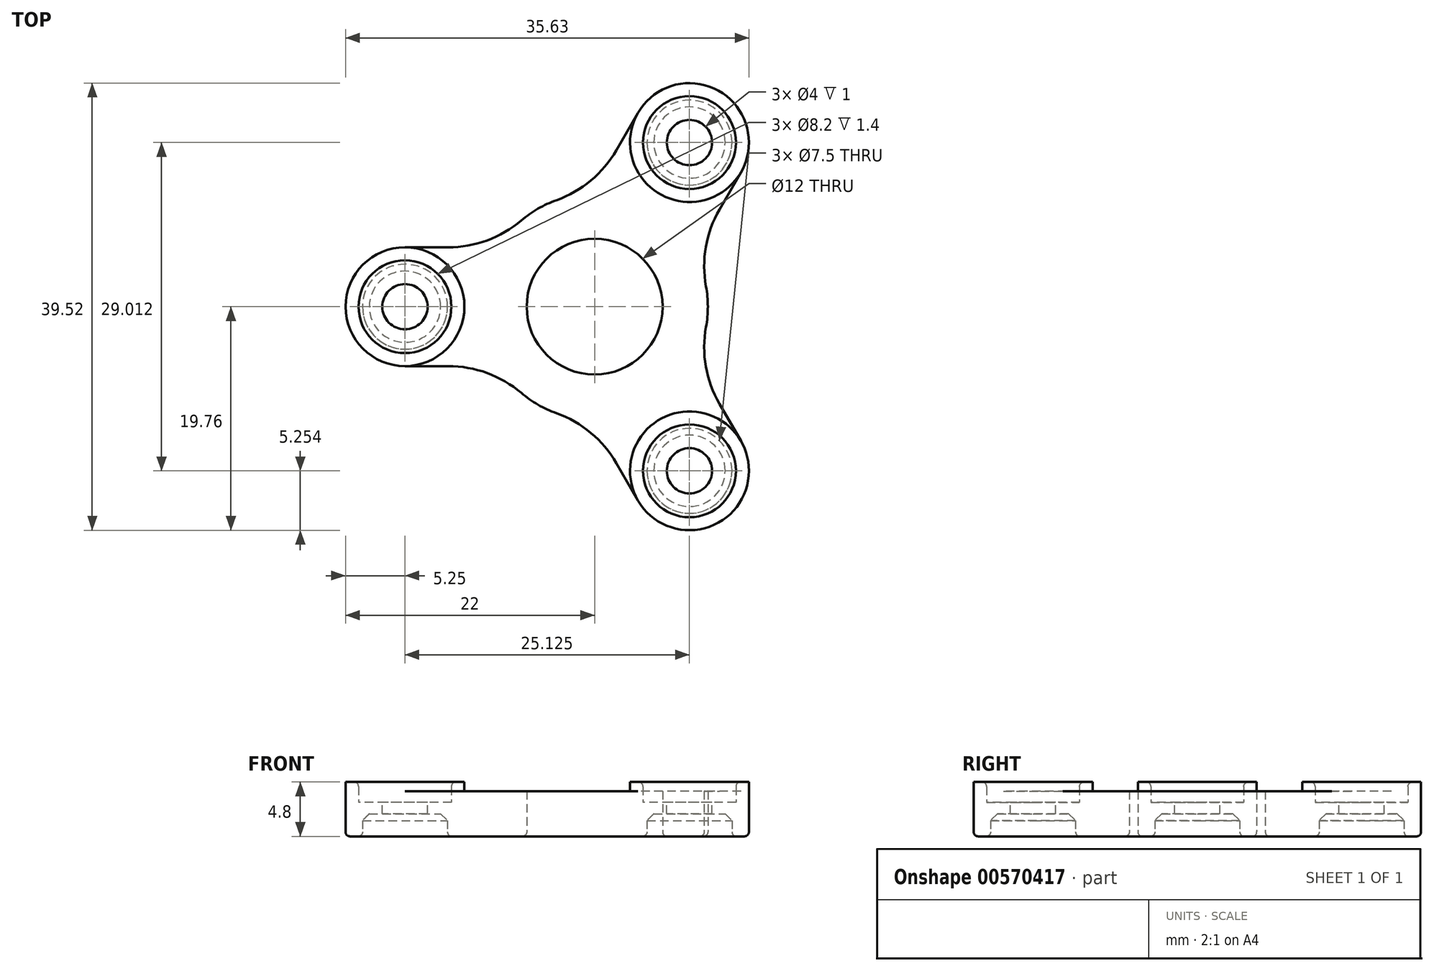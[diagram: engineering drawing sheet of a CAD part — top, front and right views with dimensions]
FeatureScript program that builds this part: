
annotation { "Feature Type Name" : "Feature", "Feature Type Description" : "" }
export const myFeature = defineFeature(function(context is Context, id is Id, definition is map)
    precondition{}
    {
        {
            var Q0;
            Q0=qCreatedBy(makeId("Top.planeOp"),FACE);
            var sketch = newSketch(context, id + "F0", { "sketchPlane" : qUnion([Q0])});
            skArc(sketch, "E0", {"start": v(-16.75, 0) * mm, "mid": v(8.38, -14.5) * mm, "end": v(8.37, 14.5) * mm, "construction": true});
            skLineSegment(sketch, "E1", {"start": v(-16.75, 0) * mm, "end": v(16.75, 0) * mm, "construction": true});
            skLineSegment(sketch, "E2", {"start": v(0, 16.75) * mm, "end": v(0, -16.75) * mm, "construction": true});
            skCircle(sketch, "E3", {"center": v(-16.75, 0) * mm, "radius": 11 * mm, "construction": true});
            skCircle(sketch, "E4", {"center": v(0, 0) * mm, "radius": 10 * mm});
            skCircle(sketch, "E5", {"center": v(-16.75, 0) * mm, "radius": 5.25 * mm});
            skPoint(sketch, "E6.center", {"position": v(-0.38, 0.43) * mm});
            skPoint(sketch, "E7.center", {"position": v(0.72, 3.29) * mm});
            skCircle(sketch, "E8", {"center": v(0, 0) * mm, "radius": 27.75 * mm, "construction": true});
            skPoint(sketch, "E9.orphan", {"position": v(-2.14, 9.77) * mm});
            skPoint(sketch, "E10.orphan", {"position": v(18.22, 8.85) * mm});
            skPoint(sketch, "E11.orphan", {"position": v(12.53, 1.01) * mm});
            skPoint(sketch, "E12.orphan", {"position": v(-7.15, -5.8) * mm});
            skPoint(sketch, "E13.orphan", {"position": v(-2.14, -9.77) * mm});
            skCircle(sketch, "E14", {"center": v(0, 0) * mm, "radius": 6 * mm});
            skArc(sketch, "E15.trimOffspring", {"start": v(2.02, 16.63) * mm, "mid": v(-9, 14.12) * mm, "end": v(-15.93, 5.19) * mm, "construction": true});
            skLineSegment(sketch, "E16", {"start": v(-16.75, 0) * mm, "end": v(-16.75, 5.25) * mm, "construction": true});
            skLineSegment(sketch, "E17", {"start": v(-16.75, 5.25) * mm, "end": v(-8.51, 5.25) * mm});
            skLineSegment(sketch, "E18.MirrorCS", {"start": v(-16.75, -5.25) * mm, "end": v(-8.51, -5.25) * mm});
            skCircle(sketch, "E19.1.0", {"center": v(8.37, -14.5) * mm, "radius": 11 * mm, "construction": true});
            skCircle(sketch, "E19.1.1", {"center": v(8.37, -14.5) * mm, "radius": 5.25 * mm});
            skLineSegment(sketch, "E19.1.2", {"start": v(12.92, -11.88) * mm, "end": v(8.8, -4.75) * mm});
            skLineSegment(sketch, "E19.1.3", {"start": v(3.83, -17.13) * mm, "end": v(-0.3, -10) * mm});
            skLineSegment(sketch, "E19.1.4", {"start": v(8.38, -14.5) * mm, "end": v(-8.38, 14.5) * mm, "construction": true});
            skCircle(sketch, "E19.2.0", {"center": v(8.37, 14.5) * mm, "radius": 11 * mm, "construction": true});
            skCircle(sketch, "E19.2.1", {"center": v(8.37, 14.5) * mm, "radius": 5.25 * mm});
            skLineSegment(sketch, "E19.2.2", {"start": v(3.83, 17.13) * mm, "end": v(-0.3, 10) * mm});
            skLineSegment(sketch, "E19.2.3", {"start": v(12.92, 11.88) * mm, "end": v(8.8, 4.75) * mm});
            skLineSegment(sketch, "E19.2.4", {"start": v(8.38, 14.5) * mm, "end": v(-8.38, -14.5) * mm, "construction": true});
            skSolve(sketch);
        }
        {
            var Q0;
            Q0=makeQuery(id+"F0.imprint","IMPRINT",FACE,{"disambiguationData":[TD([[makeQuery(id+"F0.imprint","IMPRINT",EDGE,{"derivedFrom":sQuery(id+"F0.wireOp",EDGE,"E14")}),-1.0]])]});
            var Q1;
            {var subQ0=sQuery(id+"F0.wireOp",EDGE,"E17");Q1=makeQuery(id+"F0.imprint","IMPRINT",FACE,{"disambiguationData":[TD([[makeQuery(id+"F0.imprint","IMPRINT",EDGE,{"derivedFrom":subQ0}),-1.0]])]});}
            var Q2;
            {var subQ0=sQuery(id+"F0.wireOp",EDGE,"E5");var subQ1=makeQuery(id+"F0.imprint","INTERSECT",VERTEX,{"derivedFrom":[subQ0,sQuery(id+"F0.wireOp",EDGE,"E17")]});Q2=makeQuery(id+"F0.imprint","IMPRINT",FACE,{"disambiguationData":[TD([[makeQuery(id+"F0.imprint","IMPRINT",EDGE,{"disambiguationData":[TD([[subQ1,-1.0]])],"derivedFrom":subQ0}),1.0]])]});}
            var Q3;
            {var subQ0=sQuery(id+"F0.wireOp",EDGE,"E19.2.1");var subQ1=makeQuery(id+"F0.imprint","INTERSECT",VERTEX,{"derivedFrom":[subQ0,sQuery(id+"F0.wireOp",EDGE,"E19.2.2")]});Q3=makeQuery(id+"F0.imprint","IMPRINT",FACE,{"disambiguationData":[TD([[makeQuery(id+"F0.imprint","IMPRINT",EDGE,{"disambiguationData":[TD([[subQ1,1.0]])],"derivedFrom":subQ0}),1.0]])]});}
            var Q4;
            {var subQ0=sQuery(id+"F0.wireOp",EDGE,"E19.2.2");Q4=makeQuery(id+"F0.imprint","IMPRINT",FACE,{"disambiguationData":[TD([[makeQuery(id+"F0.imprint","IMPRINT",EDGE,{"derivedFrom":subQ0}),1.0]])]});}
            var Q5;
            {var subQ0=sQuery(id+"F0.wireOp",EDGE,"E19.1.2");Q5=makeQuery(id+"F0.imprint","IMPRINT",FACE,{"disambiguationData":[TD([[makeQuery(id+"F0.imprint","IMPRINT",EDGE,{"derivedFrom":subQ0}),1.0]])]});}
            var Q6;
            {var subQ0=sQuery(id+"F0.wireOp",EDGE,"E19.1.1");var subQ1=makeQuery(id+"F0.imprint","INTERSECT",VERTEX,{"derivedFrom":[subQ0,sQuery(id+"F0.wireOp",EDGE,"E19.1.2")]});Q6=makeQuery(id+"F0.imprint","IMPRINT",FACE,{"disambiguationData":[TD([[makeQuery(id+"F0.imprint","IMPRINT",EDGE,{"disambiguationData":[TD([[subQ1,1.0]])],"derivedFrom":subQ0}),1.0]])]});}
            extrude(context, id + "F1", {"entities" : qUnion([Q0, Q1, Q2, Q3, Q4, Q5, Q6]), "depth" : 4 * mm, "offsetDistance" : 25 * mm});
        }
        {
            var Q0;
            Q0=makeQuery(id+"F1.opExtrude","CAP_FACE",FACE,{"disambiguationData":[OSD([sQuery(id+"F0.wireOp",EDGE,"E4"),sQuery(id+"F0.wireOp",EDGE,"E5"),sQuery(id+"F0.wireOp",EDGE,"E6.1.0"),sQuery(id+"F0.wireOp",EDGE,"E6.2.0"),sQuery(id+"F0.wireOp",EDGE,"E14"),sQuery(id+"F0.wireOp",EDGE,"E17"),sQuery(id+"F0.wireOp",EDGE,"E18.MirrorCS"),sQuery(id+"F0.wireOp",EDGE,"43669a28-cf5b-415e-ac1e-aebf97da9a9c.1.0"),sQuery(id+"F0.wireOp",EDGE,"43669a28-cf5b-415e-ac1e-aebf97da9a9c.1.1"),sQuery(id+"F0.wireOp",EDGE,"43669a28-cf5b-415e-ac1e-aebf97da9a9c.2.0"),sQuery(id+"F0.wireOp",EDGE,"43669a28-cf5b-415e-ac1e-aebf97da9a9c.2.1")])],"isStart":false});
            var sketch = newSketch(context, id + "F2", { "sketchPlane" : qUnion([Q0])});
            skCircle(sketch, "E20.0", {"center": v(-16.75, 0) * mm, "radius": 5.25 * mm});
            skCircle(sketch, "E21", {"center": v(-16.75, 0) * mm, "radius": 4.1 * mm});
            skCircle(sketch, "E22.1.0", {"center": v(8.37, -14.5) * mm, "radius": 5.25 * mm});
            skCircle(sketch, "E22.1.1", {"center": v(8.37, -14.5) * mm, "radius": 4.1 * mm});
            skCircle(sketch, "E22.2.0", {"center": v(8.37, 14.5) * mm, "radius": 5.25 * mm});
            skCircle(sketch, "E22.2.1", {"center": v(8.37, 14.5) * mm, "radius": 4.1 * mm});
            skPoint(sketch, "E22.center", {"position": v(0, 0) * mm});
            skCircle(sketch, "E23", {"center": v(-16.75, 0) * mm, "radius": 2 * mm});
            skCircle(sketch, "E24.1.0", {"center": v(8.37, -14.5) * mm, "radius": 2 * mm});
            skCircle(sketch, "E24.2.0", {"center": v(8.37, 14.5) * mm, "radius": 2 * mm});
            skSolve(sketch);
        }
        {
            var Q0;
            Q0=makeQuery(id+"F2.imprint","IMPRINT",FACE,{"disambiguationData":[TD([[makeQuery(id+"F2.imprint","IMPRINT",EDGE,{"derivedFrom":sQuery(id+"F2.wireOp",EDGE,"E21")}),-1.0]])]});
            var Q1;
            Q1=makeQuery(id+"F2.imprint","IMPRINT",FACE,{"disambiguationData":[TD([[makeQuery(id+"F2.imprint","IMPRINT",EDGE,{"derivedFrom":sQuery(id+"F2.wireOp",EDGE,"E22.2.0")}),1.0]])]});
            var Q2;
            Q2=makeQuery(id+"F2.imprint","IMPRINT",FACE,{"disambiguationData":[TD([[makeQuery(id+"F2.imprint","IMPRINT",EDGE,{"derivedFrom":sQuery(id+"F2.wireOp",EDGE,"E22.1.0")}),1.0]])]});
            extrude(context, id + "F3", {"entities" : qUnion([Q0, Q1, Q2]), "operationType" : NewBodyOperationType.ADD, "depth" : .8 * mm, "offsetDistance" : 25 * mm});
        }
        {
            var Q0;
            Q0=makeQuery(id+"F2.imprint","IMPRINT",FACE,{"disambiguationData":[TD([[makeQuery(id+"F2.imprint","IMPRINT",EDGE,{"derivedFrom":sQuery(id+"F2.wireOp",EDGE,"E23")}),1.0]])]});
            var Q1;
            Q1=makeQuery(id+"F2.imprint","IMPRINT",FACE,{"disambiguationData":[TD([[makeQuery(id+"F2.imprint","IMPRINT",EDGE,{"derivedFrom":sQuery(id+"F2.wireOp",EDGE,"E24.2.0")}),1.0]])]});
            var Q2;
            Q2=makeQuery(id+"F2.imprint","IMPRINT",FACE,{"disambiguationData":[TD([[makeQuery(id+"F2.imprint","IMPRINT",EDGE,{"derivedFrom":sQuery(id+"F2.wireOp",EDGE,"E24.1.0")}),1.0]])]});
            extrude(context, id + "F4", {"entities" : qUnion([Q0, Q1, Q2]), "operationType" : NewBodyOperationType.REMOVE, "endBound" : BoundingType.THROUGH_ALL, "oppositeDirection" : true, "depth" : 25 * mm, "offsetDistance" : 25 * mm});
        }
        {
            var Q0;
            Q0=makeQuery(id+"F1.opExtrude","CAP_FACE",FACE,{"disambiguationData":[OSD([sQuery(id+"F0.wireOp",EDGE,"E4"),sQuery(id+"F0.wireOp",EDGE,"E5"),sQuery(id+"F0.wireOp",EDGE,"E6.1.0"),sQuery(id+"F0.wireOp",EDGE,"E6.2.0"),sQuery(id+"F0.wireOp",EDGE,"E14"),sQuery(id+"F0.wireOp",EDGE,"E17"),sQuery(id+"F0.wireOp",EDGE,"E18.MirrorCS"),sQuery(id+"F0.wireOp",EDGE,"43669a28-cf5b-415e-ac1e-aebf97da9a9c.1.0"),sQuery(id+"F0.wireOp",EDGE,"43669a28-cf5b-415e-ac1e-aebf97da9a9c.1.1"),sQuery(id+"F0.wireOp",EDGE,"43669a28-cf5b-415e-ac1e-aebf97da9a9c.2.0"),sQuery(id+"F0.wireOp",EDGE,"43669a28-cf5b-415e-ac1e-aebf97da9a9c.2.1")])],"isStart":true});
            var sketch = newSketch(context, id + "F5", { "sketchPlane" : qUnion([Q0])});
            skCircle(sketch, "E25.0", {"center": v(-16.75, 0) * mm, "radius": 2 * mm, "construction": true});
            skCircle(sketch, "E26", {"center": v(-16.75, 0) * mm, "radius": 3.75 * mm});
            skCircle(sketch, "E27.1.0", {"center": v(8.37, -14.5) * mm, "radius": 3.75 * mm});
            skCircle(sketch, "E27.2.0", {"center": v(8.37, 14.5) * mm, "radius": 3.75 * mm});
            skPoint(sketch, "E27.center", {"position": v(0, 0) * mm});
            skSolve(sketch);
        }
        {
            var Q0;
            Q0=makeQuery(id+"F5.imprint","IMPRINT",FACE,{"disambiguationData":[TD([[makeQuery(id+"F5.imprint","IMPRINT",EDGE,{"derivedFrom":sQuery(id+"F5.wireOp",EDGE,"E26")}),1.0]])]});
            var Q1;
            Q1=makeQuery(id+"F5.imprint","IMPRINT",FACE,{"disambiguationData":[TD([[makeQuery(id+"F5.imprint","IMPRINT",EDGE,{"derivedFrom":sQuery(id+"F5.wireOp",EDGE,"E27.2.0")}),1.0]])]});
            var Q2;
            Q2=makeQuery(id+"F5.imprint","IMPRINT",FACE,{"disambiguationData":[TD([[makeQuery(id+"F5.imprint","IMPRINT",EDGE,{"derivedFrom":sQuery(id+"F5.wireOp",EDGE,"E27.1.0")}),1.0]])]});
            extrude(context, id + "F6", {"entities" : qUnion([Q0, Q1, Q2]), "operationType" : NewBodyOperationType.REMOVE, "oppositeDirection" : true, "depth" : 2 * mm, "offsetDistance" : 25 * mm});
        }
        {
            var Q0;
            Q0=makeQuery(id+"F6.boolean.opBoolean","COPY",EDGE,{"derivedFrom":makeQuery(id+"F6.opExtrude","CAP_EDGE",EDGE,{"disambiguationData":[OSD([sQuery(id+"F5.wireOp",EDGE,"E27.2.0")])],"isStart":false})});
            var Q1;
            Q1=makeQuery(id+"F6.boolean.opBoolean","COPY",EDGE,{"derivedFrom":makeQuery(id+"F6.opExtrude","CAP_EDGE",EDGE,{"disambiguationData":[OSD([sQuery(id+"F5.wireOp",EDGE,"E26")])],"isStart":false})});
            var Q2;
            Q2=makeQuery(id+"F6.boolean.opBoolean","COPY",EDGE,{"derivedFrom":makeQuery(id+"F6.opExtrude","CAP_EDGE",EDGE,{"disambiguationData":[OSD([sQuery(id+"F5.wireOp",EDGE,"E27.1.0")])],"isStart":false})});
            chamfer(context, id + "F7", {"entities" : qUnion([Q0, Q1, Q2]), "width" : .6 * mm, "tangentPropagation" : true});
        }
        {
            var Q0;
            Q0=makeQuery(id+"F3.boolean.opBoolean","SPLIT",FACE,{"disambiguationData":[TD([makeQuery(id+"F3.opExtrude","SWEPT_FACE",FACE,{"disambiguationData":[OSD([sQuery(id+"F2.wireOp",EDGE,"E21")])]})])],"derivedFrom":makeQuery(id+"F1.opExtrude","CAP_FACE",FACE,{"disambiguationData":[OSD([sQuery(id+"F0.wireOp",EDGE,"E4"),sQuery(id+"F0.wireOp",EDGE,"E5"),sQuery(id+"F0.wireOp",EDGE,"E6.1.0"),sQuery(id+"F0.wireOp",EDGE,"E6.2.0"),sQuery(id+"F0.wireOp",EDGE,"E14"),sQuery(id+"F0.wireOp",EDGE,"E17"),sQuery(id+"F0.wireOp",EDGE,"E18.MirrorCS"),sQuery(id+"F0.wireOp",EDGE,"43669a28-cf5b-415e-ac1e-aebf97da9a9c.1.0"),sQuery(id+"F0.wireOp",EDGE,"43669a28-cf5b-415e-ac1e-aebf97da9a9c.1.1"),sQuery(id+"F0.wireOp",EDGE,"43669a28-cf5b-415e-ac1e-aebf97da9a9c.2.0"),sQuery(id+"F0.wireOp",EDGE,"43669a28-cf5b-415e-ac1e-aebf97da9a9c.2.1")])],"isStart":false})});
            var Q1;
            Q1=makeQuery(id+"F3.boolean.opBoolean","SPLIT",FACE,{"disambiguationData":[TD([makeQuery(id+"F3.opExtrude","SWEPT_FACE",FACE,{"disambiguationData":[OSD([sQuery(id+"F2.wireOp",EDGE,"E22.2.1")])]})])],"derivedFrom":makeQuery(id+"F1.opExtrude","CAP_FACE",FACE,{"disambiguationData":[OSD([sQuery(id+"F0.wireOp",EDGE,"E4"),sQuery(id+"F0.wireOp",EDGE,"E5"),sQuery(id+"F0.wireOp",EDGE,"E6.1.0"),sQuery(id+"F0.wireOp",EDGE,"E6.2.0"),sQuery(id+"F0.wireOp",EDGE,"E14"),sQuery(id+"F0.wireOp",EDGE,"E17"),sQuery(id+"F0.wireOp",EDGE,"E18.MirrorCS"),sQuery(id+"F0.wireOp",EDGE,"43669a28-cf5b-415e-ac1e-aebf97da9a9c.1.0"),sQuery(id+"F0.wireOp",EDGE,"43669a28-cf5b-415e-ac1e-aebf97da9a9c.1.1"),sQuery(id+"F0.wireOp",EDGE,"43669a28-cf5b-415e-ac1e-aebf97da9a9c.2.0"),sQuery(id+"F0.wireOp",EDGE,"43669a28-cf5b-415e-ac1e-aebf97da9a9c.2.1")])],"isStart":false})});
            var Q2;
            Q2=makeQuery(id+"F3.boolean.opBoolean","SPLIT",FACE,{"disambiguationData":[TD([makeQuery(id+"F3.opExtrude","SWEPT_FACE",FACE,{"disambiguationData":[OSD([sQuery(id+"F2.wireOp",EDGE,"E22.1.1")])]})])],"derivedFrom":makeQuery(id+"F1.opExtrude","CAP_FACE",FACE,{"disambiguationData":[OSD([sQuery(id+"F0.wireOp",EDGE,"E4"),sQuery(id+"F0.wireOp",EDGE,"E5"),sQuery(id+"F0.wireOp",EDGE,"E6.1.0"),sQuery(id+"F0.wireOp",EDGE,"E6.2.0"),sQuery(id+"F0.wireOp",EDGE,"E14"),sQuery(id+"F0.wireOp",EDGE,"E17"),sQuery(id+"F0.wireOp",EDGE,"E18.MirrorCS"),sQuery(id+"F0.wireOp",EDGE,"43669a28-cf5b-415e-ac1e-aebf97da9a9c.1.0"),sQuery(id+"F0.wireOp",EDGE,"43669a28-cf5b-415e-ac1e-aebf97da9a9c.1.1"),sQuery(id+"F0.wireOp",EDGE,"43669a28-cf5b-415e-ac1e-aebf97da9a9c.2.0"),sQuery(id+"F0.wireOp",EDGE,"43669a28-cf5b-415e-ac1e-aebf97da9a9c.2.1")])],"isStart":false})});
            extrude(context, id + "F8", {"entities" : qUnion([Q0, Q1, Q2]), "operationType" : NewBodyOperationType.REMOVE, "oppositeDirection" : true, "depth" : 1 * mm, "offsetDistance" : 25 * mm});
        }
        {
            var Q0;
            Q0=makeQuery(id+"F1.opExtrude","SWEPT_EDGE",EDGE,{"disambiguationData":[OSD([sQuery(id+"F0.wireOp",EDGE,"E4"),sQuery(id+"F0.wireOp",EDGE,"E18.MirrorCS")])]});
            var Q1;
            Q1=makeQuery(id+"F1.opExtrude","SWEPT_EDGE",EDGE,{"disambiguationData":[OSD([sQuery(id+"F0.wireOp",EDGE,"E4"),sQuery(id+"F0.wireOp",EDGE,"43669a28-cf5b-415e-ac1e-aebf97da9a9c.1.0")])]});
            var Q2;
            Q2=makeQuery(id+"F1.opExtrude","SWEPT_EDGE",EDGE,{"disambiguationData":[OSD([sQuery(id+"F0.wireOp",EDGE,"E4"),sQuery(id+"F0.wireOp",EDGE,"43669a28-cf5b-415e-ac1e-aebf97da9a9c.1.1")])]});
            var Q3;
            Q3=makeQuery(id+"F1.opExtrude","SWEPT_EDGE",EDGE,{"disambiguationData":[OSD([sQuery(id+"F0.wireOp",EDGE,"E4"),sQuery(id+"F0.wireOp",EDGE,"43669a28-cf5b-415e-ac1e-aebf97da9a9c.2.0")])]});
            var Q4;
            Q4=makeQuery(id+"F1.opExtrude","SWEPT_EDGE",EDGE,{"disambiguationData":[OSD([sQuery(id+"F0.wireOp",EDGE,"E4"),sQuery(id+"F0.wireOp",EDGE,"E17")])]});
            var Q5;
            Q5=makeQuery(id+"F1.opExtrude","SWEPT_EDGE",EDGE,{"disambiguationData":[OSD([sQuery(id+"F0.wireOp",EDGE,"E4"),sQuery(id+"F0.wireOp",EDGE,"43669a28-cf5b-415e-ac1e-aebf97da9a9c.2.1")])]});
            fillet(context, id + "F9", {"entities" : qUnion([Q0, Q1, Q2, Q3, Q4, Q5]), "radius" : 10 * mm, "tangentPropagation" : true, "allowEdgeOverflow" : false});
        }
        {
            var Q0;
            {var subQ0=sQuery(id+"F0.wireOp",EDGE,"E18.MirrorCS");var subQ1=sQuery(id+"F0.wireOp",EDGE,"E17");var subQ2=sQuery(id+"F0.wireOp",EDGE,"E14");var subQ3=sQuery(id+"F0.wireOp",EDGE,"E6.2.0");var subQ4=sQuery(id+"F0.wireOp",EDGE,"E6.1.0");var subQ5=sQuery(id+"F0.wireOp",EDGE,"43669a28-cf5b-415e-ac1e-aebf97da9a9c.1.0");var subQ6=sQuery(id+"F0.wireOp",EDGE,"E4");var subQ7=sQuery(id+"F0.wireOp",EDGE,"43669a28-cf5b-415e-ac1e-aebf97da9a9c.2.1");var subQ8=sQuery(id+"F0.wireOp",EDGE,"E5");var subQ9=sQuery(id+"F0.wireOp",EDGE,"43669a28-cf5b-415e-ac1e-aebf97da9a9c.1.1");var subQ10=sQuery(id+"F0.wireOp",EDGE,"43669a28-cf5b-415e-ac1e-aebf97da9a9c.2.0");Q0=makeQuery(id+"F3.boolean.opBoolean","SPLIT",FACE,{"disambiguationData":[TD([makeQuery(id+"F1.opExtrude","SWEPT_FACE",FACE,{"disambiguationData":[OSD([subQ8])]})])],"derivedFrom":makeQuery(id+"F1.opExtrude","CAP_FACE",FACE,{"disambiguationData":[OSD([subQ6,subQ8,subQ4,subQ3,subQ2,subQ1,subQ0,subQ5,subQ9,subQ10,subQ7])],"isStart":false})});}
            var Q1;
            Q1=makeQuery(id+"F1.opExtrude","CAP_FACE",FACE,{"disambiguationData":[OSD([sQuery(id+"F0.wireOp",EDGE,"E4"),sQuery(id+"F0.wireOp",EDGE,"E5"),sQuery(id+"F0.wireOp",EDGE,"E6.1.0"),sQuery(id+"F0.wireOp",EDGE,"E6.2.0"),sQuery(id+"F0.wireOp",EDGE,"E14"),sQuery(id+"F0.wireOp",EDGE,"E17"),sQuery(id+"F0.wireOp",EDGE,"E18.MirrorCS"),sQuery(id+"F0.wireOp",EDGE,"43669a28-cf5b-415e-ac1e-aebf97da9a9c.1.0"),sQuery(id+"F0.wireOp",EDGE,"43669a28-cf5b-415e-ac1e-aebf97da9a9c.1.1"),sQuery(id+"F0.wireOp",EDGE,"43669a28-cf5b-415e-ac1e-aebf97da9a9c.2.0"),sQuery(id+"F0.wireOp",EDGE,"43669a28-cf5b-415e-ac1e-aebf97da9a9c.2.1")])],"isStart":true});
            var Q2;
            Q2=makeQuery(id+"F3.opExtrude","CAP_EDGE",EDGE,{"disambiguationData":[OSD([sQuery(id+"F2.wireOp",EDGE,"E21")])],"isStart":false});
            var Q3;
            Q3=makeQuery(id+"F3.opExtrude","CAP_EDGE",EDGE,{"disambiguationData":[OSD([sQuery(id+"F2.wireOp",EDGE,"E22.1.1")])],"isStart":false});
            var Q4;
            Q4=makeQuery(id+"F3.opExtrude","CAP_EDGE",EDGE,{"disambiguationData":[OSD([sQuery(id+"F2.wireOp",EDGE,"E22.2.1")])],"isStart":false});
            fillet(context, id + "F10", {"entities" : qUnion([Q0, Q1, Q2, Q3, Q4]), "radius" : .4 * mm, "tangentPropagation" : true, "allowEdgeOverflow" : false});
        }
    });
